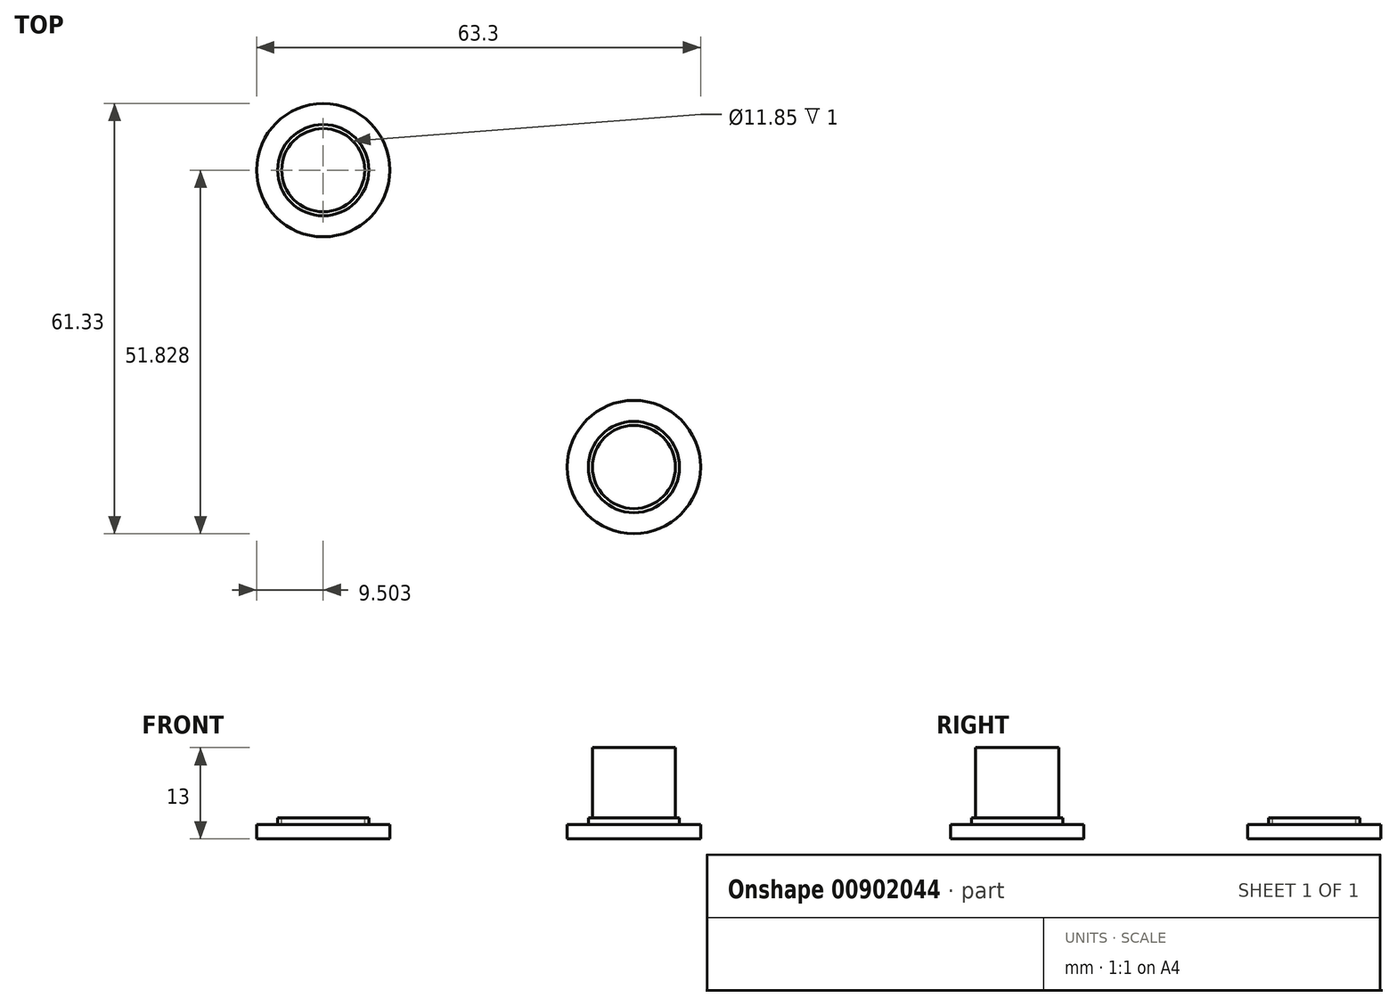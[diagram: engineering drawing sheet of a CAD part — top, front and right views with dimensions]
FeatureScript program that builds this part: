
annotation { "Feature Type Name" : "Feature", "Feature Type Description" : "" }
export const myFeature = defineFeature(function(context is Context, id is Id, definition is map)
    precondition{}
    {
        {
            var Q0;
            Q0=qCreatedBy(makeId("Top.planeOp"),FACE);
            var sketch = newSketch(context, id + "F0", { "sketchPlane" : qUnion([Q0])});
            skCircle(sketch, "E0", {"center": v(0, 0) * mm, "radius": 9.5 * mm});
            skSolve(sketch);
        }
        {
            var Q0;
            Q0=makeQuery(id+"F0.imprint","IMPRINT",FACE,{"disambiguationData":[TD([[makeQuery(id+"F0.imprint","IMPRINT",EDGE,{"derivedFrom":sQuery(id+"F0.wireOp",EDGE,"E0")}),1.0]])]});
            extrude(context, id + "F1", {"entities" : qUnion([Q0]), "depth" : 2 * mm, "offsetDistance" : 25 * mm});
        }
        {
            var Q0;
            Q0=makeQuery(id+"F1.opExtrude","CAP_FACE",FACE,{"disambiguationData":[OSD([sQuery(id+"F0.wireOp",EDGE,"E0")])],"isStart":false});
            var sketch = newSketch(context, id + "F2", { "sketchPlane" : qUnion([Q0])});
            skCircle(sketch, "E1", {"center": v(0, 0) * mm, "radius": 6.5 * mm});
            skSolve(sketch);
        }
        {
            var Q0;
            Q0=makeQuery(id+"F2.imprint","IMPRINT",FACE,{"disambiguationData":[TD([[makeQuery(id+"F2.imprint","IMPRINT",EDGE,{"derivedFrom":sQuery(id+"F2.wireOp",EDGE,"E1")}),1.0]])]});
            extrude(context, id + "F3", {"entities" : qUnion([Q0]), "operationType" : NewBodyOperationType.ADD, "depth" : 1 * mm, "offsetDistance" : 25 * mm});
        }
        {
            var Q0;
            Q0=makeQuery(id+"F3.opExtrude","CAP_FACE",FACE,{"disambiguationData":[OSD([sQuery(id+"F2.wireOp",EDGE,"E1")])],"isStart":false});
            var sketch = newSketch(context, id + "F4", { "sketchPlane" : qUnion([Q0])});
            skCircle(sketch, "E2", {"center": v(0, 0) * mm, "radius": 5.92 * mm});
            skSolve(sketch);
        }
        {
            var Q0;
            Q0=qSketchRegion(id+"F4",true);
            extrude(context, id + "F5", {"entities" : qUnion([Q0]), "operationType" : NewBodyOperationType.ADD, "depth" : 10 * mm, "offsetDistance" : 25 * mm});
        }
        {
            var Q0;
            Q0=qCreatedBy(makeId("Top.planeOp"),FACE);
            var sketch = newSketch(context, id + "F6", { "sketchPlane" : qUnion([Q0])});
            skCircle(sketch, "E3", {"center": v(-44.3, 42.33) * mm, "radius": 9.5 * mm});
            skSolve(sketch);
        }
        {
            var Q0;
            Q0=makeQuery(id+"F6.imprint","IMPRINT",FACE,{"disambiguationData":[TD([[makeQuery(id+"F6.imprint","IMPRINT",EDGE,{"derivedFrom":sQuery(id+"F6.wireOp",EDGE,"E3")}),1.0]])]});
            extrude(context, id + "F7", {"entities" : qUnion([Q0]), "depth" : 2 * mm, "offsetDistance" : 25 * mm});
        }
        {
            var Q0;
            Q0=makeQuery(id+"F7.opExtrude","CAP_FACE",FACE,{"disambiguationData":[OSD([sQuery(id+"F6.wireOp",EDGE,"E3")])],"isStart":false});
            var sketch = newSketch(context, id + "F8", { "sketchPlane" : qUnion([Q0])});
            skCircle(sketch, "E4", {"center": v(-44.3, 42.33) * mm, "radius": 6.5 * mm});
            skSolve(sketch);
        }
        {
            var Q0;
            Q0=makeQuery(id+"F8.imprint","IMPRINT",FACE,{"disambiguationData":[TD([[makeQuery(id+"F8.imprint","IMPRINT",EDGE,{"derivedFrom":sQuery(id+"F8.wireOp",EDGE,"E4")}),1.0]])]});
            extrude(context, id + "F9", {"entities" : qUnion([Q0]), "operationType" : NewBodyOperationType.ADD, "depth" : 1 * mm, "offsetDistance" : 25 * mm});
        }
        {
            var Q0;
            Q0=makeQuery(id+"F9.opExtrude","CAP_FACE",FACE,{"disambiguationData":[OSD([sQuery(id+"F8.wireOp",EDGE,"E4")])],"isStart":false});
            var sketch = newSketch(context, id + "F10", { "sketchPlane" : qUnion([Q0])});
            skCircle(sketch, "E5", {"center": v(-44.3, 42.33) * mm, "radius": 5.93 * mm});
            skSolve(sketch);
        }
        {
            var Q0;
            Q0=makeQuery(id+"F10.imprint","IMPRINT",FACE,{"disambiguationData":[TD([[makeQuery(id+"F10.imprint","IMPRINT",EDGE,{"derivedFrom":sQuery(id+"F10.wireOp",EDGE,"E5")}),1.0]])]});
            extrude(context, id + "F11", {"entities" : qUnion([Q0]), "operationType" : NewBodyOperationType.REMOVE, "oppositeDirection" : true, "depth" : 1 * mm, "offsetDistance" : 25 * mm});
        }
    });
